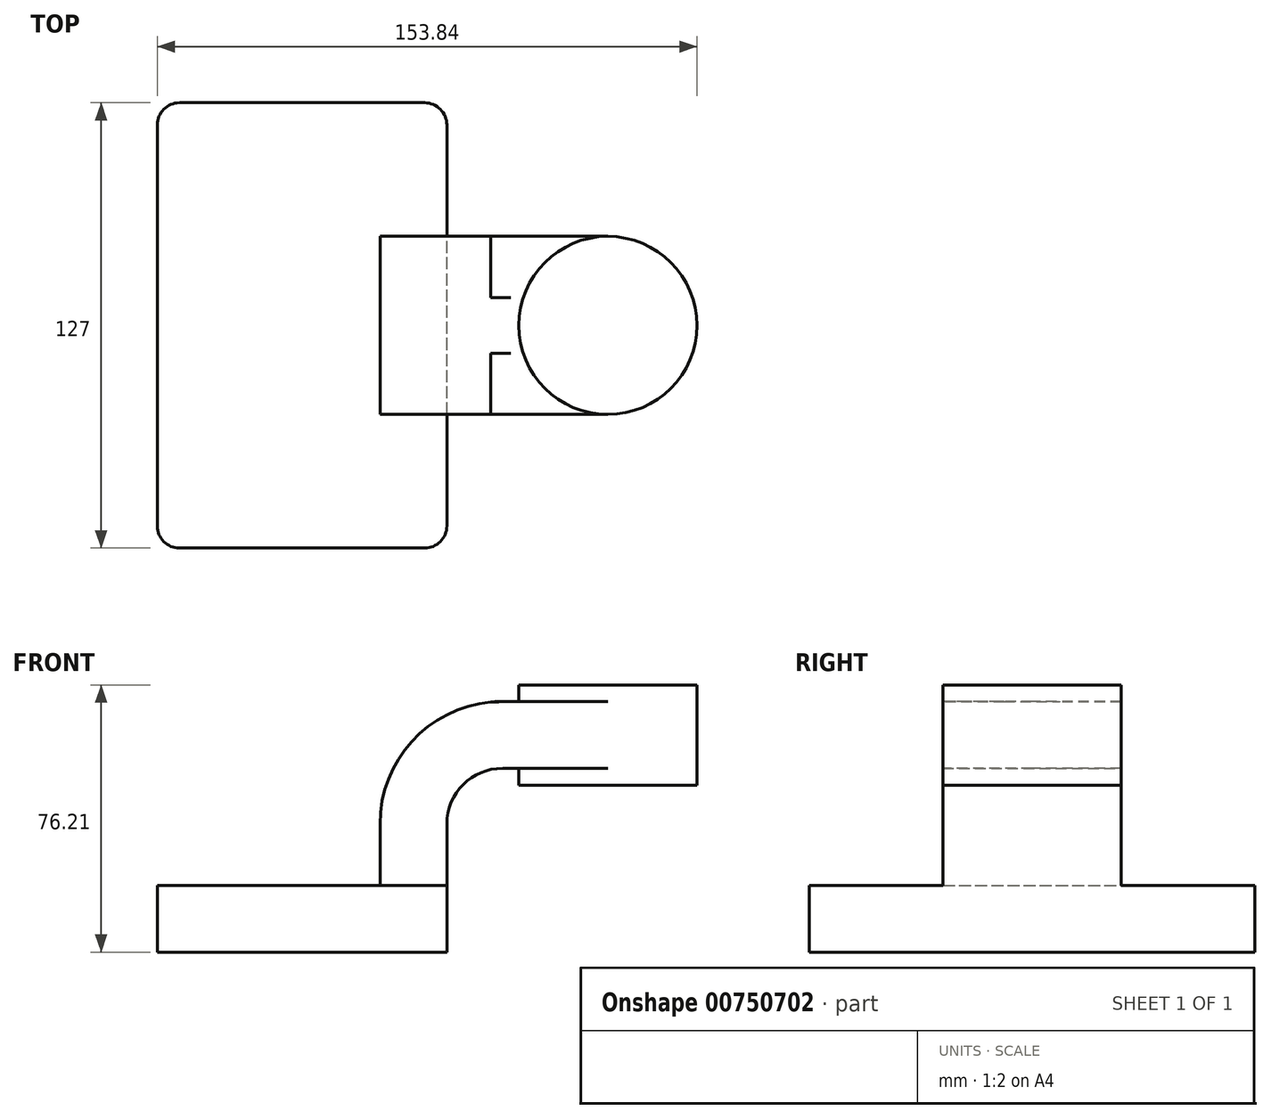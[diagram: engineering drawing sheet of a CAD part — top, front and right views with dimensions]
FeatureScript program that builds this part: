
annotation { "Feature Type Name" : "Feature", "Feature Type Description" : "" }
export const myFeature = defineFeature(function(context is Context, id is Id, definition is map)
    precondition{}
    {
        {
            var Q0;
            Q0=qCreatedBy(makeId("Front.planeOp"),FACE);
            var sketch = newSketch(context, id + "F0", { "sketchPlane" : qUnion([Q0])});
            skLineSegment(sketch, "E0.bottom", {"start": v(-41.28, -9.53) * mm, "end": v(41.28, -9.53) * mm});
            skLineSegment(sketch, "E0.top", {"start": v(-41.28, 9.53) * mm, "end": v(41.28, 9.53) * mm});
            skLineSegment(sketch, "E0.left", {"start": v(-41.28, -9.53) * mm, "end": v(-41.28, 9.53) * mm});
            skLineSegment(sketch, "E0.right", {"start": v(41.28, -9.53) * mm, "end": v(41.28, 9.53) * mm});
            skPoint(sketch, "E0.middle", {"position": v(0, 0) * mm});
            skLineSegment(sketch, "E1.bottom", {"start": v(61.77, 38.1) * mm, "end": v(112.57, 38.1) * mm});
            skLineSegment(sketch, "E1.top", {"start": v(61.77, 66.67) * mm, "end": v(112.57, 66.67) * mm});
            skLineSegment(sketch, "E1.left", {"start": v(61.77, 38.1) * mm, "end": v(61.77, 66.67) * mm});
            skLineSegment(sketch, "E1.right", {"start": v(112.57, 38.1) * mm, "end": v(112.57, 66.67) * mm});
            skPoint(sketch, "E1.middle", {"position": v(87.17, 52.39) * mm});
            skLineSegment(sketch, "E2", {"start": v(41.27, 9.53) * mm, "end": v(41.27, 27) * mm});
            skArc(sketch, "E3", {"start": v(41.27, 27) * mm, "mid": v(45.92, 38.23) * mm, "end": v(57.15, 42.88) * mm});
            skLineSegment(sketch, "E4", {"start": v(57.15, 42.88) * mm, "end": v(87.17, 42.88) * mm});
            skLineSegment(sketch, "E5.0", {"start": v(57.15, 61.93) * mm, "end": v(87.17, 61.93) * mm});
            skArc(sketch, "E5.1", {"start": v(22.23, 27) * mm, "mid": v(32.45, 51.7) * mm, "end": v(57.15, 61.93) * mm});
            skLineSegment(sketch, "E5.2", {"start": v(22.23, 9.52) * mm, "end": v(22.23, 27) * mm});
            skLineSegment(sketch, "E6", {"start": v(87.17, 38.1) * mm, "end": v(87.17, 66.67) * mm});
            skFitSpline(sketch, "E7", {"points": [v(-41.28, 9.53) * mm, v(61.77, 61.93) * mm], "startDerivative": vector(61.35, 93.24) * mm, "endDerivative": vector(136.54, -1.13) * mm});
            skSolve(sketch);
        }
        {
            var Q0;
            Q0=makeQuery(id+"F0.imprint","IMPRINT",FACE,{"disambiguationData":[TD([[makeQuery(id+"F0.imprint","IMPRINT",EDGE,{"derivedFrom":sQuery(id+"F0.wireOp",EDGE,"E0.bottom")}),1.0]])]});
            extrude(context, id + "F1", {"entities" : qUnion([Q0]), "endBound" : BoundingType.SYMMETRIC, "depth" : 127 * mm, "offsetDistance" : 25.4 * mm});
        }
        {
            var Q0;
            {var subQ1=sQuery(id+"F0.wireOp",EDGE,"E2");Q0=makeQuery(id+"F0.imprint","IMPRINT",FACE,{"disambiguationData":[TD([[makeQuery(id+"F0.imprint","IMPRINT",EDGE,{"derivedFrom":subQ1}),1.0]])]});}
            var Q1;
            {var subQ0=sQuery(id+"F0.wireOp",EDGE,"E4");var subQ1=sQuery(id+"F0.wireOp",EDGE,"E1.left");var subQ2=makeQuery(id+"F0.imprint","INTERSECT",VERTEX,{"derivedFrom":[subQ1,subQ0]});Q1=makeQuery(id+"F0.imprint","IMPRINT",FACE,{"disambiguationData":[TD([[makeQuery(id+"F0.imprint","IMPRINT",EDGE,{"disambiguationData":[TD([[subQ2,-1.0]])],"derivedFrom":subQ1}),-1.0]])]});}
            extrude(context, id + "F2", {"entities" : qUnion([Q0, Q1]), "operationType" : NewBodyOperationType.ADD, "endBound" : BoundingType.SYMMETRIC, "depth" : 50.8 * mm, "offsetDistance" : 25.4 * mm});
        }
        {
            var Q0;
            {var subQ0=sQuery(id+"F0.wireOp",EDGE,"E5.1");Q0=makeQuery(id+"F0.imprint","IMPRINT",FACE,{"disambiguationData":[TD([[makeQuery(id+"F0.imprint","IMPRINT",EDGE,{"derivedFrom":subQ0}),1.0]])]});}
            extrude(context, id + "F3", {"entities" : qUnion([Q0]), "operationType" : NewBodyOperationType.ADD, "endBound" : BoundingType.SYMMETRIC, "depth" : 15.88 * mm, "offsetDistance" : 25.4 * mm});
        }
        {
            var Q0;
            {var subQ0=sQuery(id+"F0.wireOp",EDGE,"E1.right");Q0=makeQuery(id+"F0.imprint","IMPRINT",FACE,{"disambiguationData":[TD([[makeQuery(id+"F0.imprint","IMPRINT",EDGE,{"derivedFrom":subQ0}),1.0]])]});}
            var Q1;
            Q1=sQuery(id+"F0.wireOp",EDGE,"E6");
            revolve(context, id + "F4", {"operationType" : NewBodyOperationType.ADD, "surfaceOperationType" : NewSurfaceOperationType.NEW, "entities" : qUnion([Q0]), "axis" : qUnion([Q1]), "revolveType" : RevolveType.FULL});
        }
        {
            var Q0;
            Q0=makeQuery(id+"F1.opExtrude","CAP_EDGE",EDGE,{"disambiguationData":[OSD([sQuery(id+"F0.wireOp",EDGE,"E0.left")])],"isStart":false});
            var Q1;
            Q1=makeQuery(id+"F1.opExtrude","CAP_EDGE",EDGE,{"disambiguationData":[OSD([sQuery(id+"F0.wireOp",EDGE,"E0.right")])],"isStart":false});
            var Q2;
            Q2=makeQuery(id+"F1.opExtrude","CAP_EDGE",EDGE,{"disambiguationData":[OSD([sQuery(id+"F0.wireOp",EDGE,"E0.right")])],"isStart":true});
            var Q3;
            Q3=makeQuery(id+"F1.opExtrude","CAP_EDGE",EDGE,{"disambiguationData":[OSD([sQuery(id+"F0.wireOp",EDGE,"E0.left")])],"isStart":true});
            fillet(context, id + "F5", {"entities" : qUnion([Q0, Q1, Q2, Q3]), "radius" : 6.35 * mm, "tangentPropagation" : true, "allowEdgeOverflow" : false});
        }
    });
